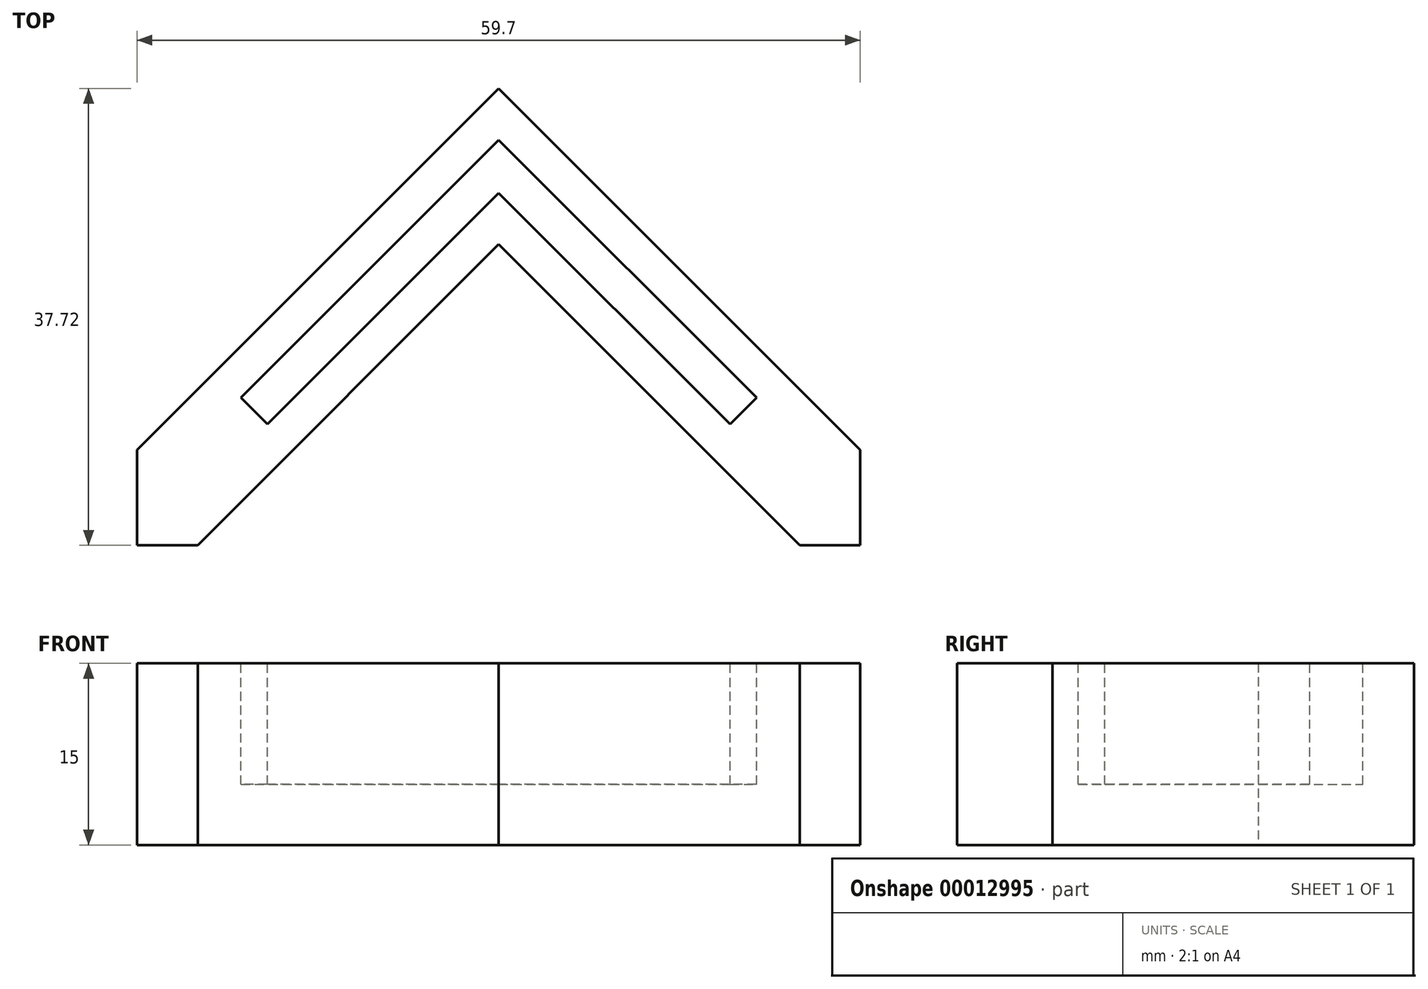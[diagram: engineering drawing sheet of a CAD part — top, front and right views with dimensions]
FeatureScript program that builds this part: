
annotation { "Feature Type Name" : "Feature", "Feature Type Description" : "" }
export const myFeature = defineFeature(function(context is Context, id is Id, definition is map)
    precondition{}
    {
        {
            var Q0;
            Q0=qCreatedBy(makeId("Top.planeOp"),FACE);
            var sketch = newSketch(context, id + "F0", { "sketchPlane" : qUnion([Q0])});
            skLineSegment(sketch, "E0", {"start": v(0, 29.1) * mm, "end": v(19.1, 10) * mm, "construction": true});
            skLineSegment(sketch, "E1", {"start": v(19.1, 10) * mm, "end": v(21.28, 12.2) * mm, "construction": true});
            skLineSegment(sketch, "E2", {"start": v(21.28, 12.2) * mm, "end": v(0, 33.48) * mm, "construction": true});
            skLineSegment(sketch, "E3", {"start": v(0, 37.72) * mm, "end": v(29.85, 7.87) * mm});
            skLineSegment(sketch, "E4", {"start": v(29.85, 7.87) * mm, "end": v(29.85, 0) * mm});
            skLineSegment(sketch, "E5", {"start": v(29.85, 0) * mm, "end": v(24.85, 0) * mm});
            skLineSegment(sketch, "E6", {"start": v(24.85, 0) * mm, "end": v(0, 24.85) * mm});
            skLineSegment(sketch, "E7.MirrorCS", {"start": v(0, 37.72) * mm, "end": v(-29.85, 7.87) * mm});
            skLineSegment(sketch, "E8.MirrorCS", {"start": v(-29.85, 7.87) * mm, "end": v(-29.85, 0) * mm});
            skLineSegment(sketch, "E9.MirrorCS", {"start": v(-24.85, 0) * mm, "end": v(0, 24.85) * mm});
            skLineSegment(sketch, "E10.MirrorCS", {"start": v(-29.85, 0) * mm, "end": v(-24.85, 0) * mm});
            skSolve(sketch);
        }
        {
            var Q0;
            Q0=makeQuery(id+"F0.imprint","IMPRINT",FACE,{"disambiguationData":[TD([[makeQuery(id+"F0.imprint","IMPRINT",EDGE,{"derivedFrom":sQuery(id+"F0.wireOp",EDGE,"E3")}),-1.0]])]});
            extrude(context, id + "F1", {"entities" : qUnion([Q0]), "depth" : 15 * mm});
        }
        {
            var Q0;
            Q0=makeQuery(id+"F1.opExtrude","CAP_FACE",FACE,{"disambiguationData":[OSD([sQuery(id+"F0.wireOp",EDGE,"E3"),sQuery(id+"F0.wireOp",EDGE,"E4"),sQuery(id+"F0.wireOp",EDGE,"E5"),sQuery(id+"F0.wireOp",EDGE,"E6"),sQuery(id+"F0.wireOp",EDGE,"E7.MirrorCS"),sQuery(id+"F0.wireOp",EDGE,"E8.MirrorCS"),sQuery(id+"F0.wireOp",EDGE,"E9.MirrorCS"),sQuery(id+"F0.wireOp",EDGE,"E10.MirrorCS")])],"isStart":false});
            var sketch = newSketch(context, id + "F2", { "sketchPlane" : qUnion([Q0])});
            skLineSegment(sketch, "E11", {"start": v(21.28, 12.2) * mm, "end": v(0, 33.48) * mm});
            skLineSegment(sketch, "E12", {"start": v(19.1, 10) * mm, "end": v(21.28, 12.2) * mm});
            skLineSegment(sketch, "E13", {"start": v(0, 29.1) * mm, "end": v(19.1, 10) * mm});
            skLineSegment(sketch, "E14.MirrorCS", {"start": v(0, 29.1) * mm, "end": v(-19.1, 10) * mm});
            skLineSegment(sketch, "E15.MirrorCS", {"start": v(-21.28, 12.2) * mm, "end": v(0, 33.48) * mm});
            skLineSegment(sketch, "E16.MirrorCS", {"start": v(-19.1, 10) * mm, "end": v(-21.28, 12.2) * mm});
            skSolve(sketch);
        }
        {
            var Q0;
            Q0=makeQuery(id+"F2.imprint","IMPRINT",FACE,{"disambiguationData":[TD([[makeQuery(id+"F2.imprint","IMPRINT",EDGE,{"derivedFrom":sQuery(id+"F2.wireOp",EDGE,"E11")}),1.0]])]});
            extrude(context, id + "F3", {"entities" : qUnion([Q0]), "operationType" : NewBodyOperationType.REMOVE, "oppositeDirection" : true, "depth" : 10 * mm});
        }
    });
